# Revit family: 2059970 Sylvania Lighting Fixture BEACON MUSE TUNE II LS3 SSC01 BLACK
name_source: partatom
category: Generic Models
revit_build: Autodesk Revit 2017 (Build: 20190507_1515(x64)
units: mm (PartAtom-declared; Revit-internal decimal feet)

## family parameters
Can host rebar = No
Cut with Voids When Loaded = No
Host = Face
OmniClass Number = 23.80.70.00
OmniClass Title = Lighting
Part Type = Normal
Room Calculation Point = No
Round Connector Dimension = Use Diameter
Shared = No

## types (1)
- 2059970 BEACON MUSE TUNE II LS3 SSC01 BLACK
    Assembly Code = D5020200
    Cost = 0 $
    Default Elevation = 1219 mm
    Description = Integrated LED spotlight, Black - RAL9005 unique soft-touch ring, adjustable beam angle from a 8° spot to a 40° flood, compact and minimalist design, ideal for retail, display, museum and gallery applications, die-cast aluminium body, passive cooling heatsink. Beam angle: 8° spot to 40° flood,color temperature: 1800-6500K Tuneable white , total system power: 18W, total fixture output: 102/163 lm, LOR: 100%, colour rendering: CRI: 93 typical, LED Chromaticity: 3 step MacAdam ellipse, lifetime: >70000 hours at L70B50, energy class: A++, A+, A, IR/UV free light source without heat radiation, operating voltage: 220-240V / 50-60Hz, electronic driver, dimmable and tuneable via SylSmart SSC Bluetooth, power factor: 0.9, electrical protection: Class II, Lytespan 3 - Three Circuit Adaptor suitable for Concord Lytespan track, ingress protection rating: IP20, suitable for internal environment only, horizontal rotation: 355°, vertical tilt: 90°, dimensions: Ø80x140x216mm, weight: 0.96kg.
    Height = 200 mm  [stored 0.656168 ft]
    Keynote = IP20
    Length = 157 mm
    Manufacturer = 0
    Material_1_FEILO = <By Category>
    Material_2_FEILO = <By Category>
    Material_3_FEILO = <By Category>
    Material_4_FEILO = <By Category>
    Model = BEACON MUSE TUNE II LS3 SSC01 BLACK
    Type Image = <None>
    URL = 23.80.70.00
    Width = 140 mm

note: [stored X ft] marks values corroborated as IEEE doubles in the binary element streams (Revit-internal decimal feet)

## geometry (parser evidence)
native form markers: Sweep x8
no freeform markers — native parametric forms only
